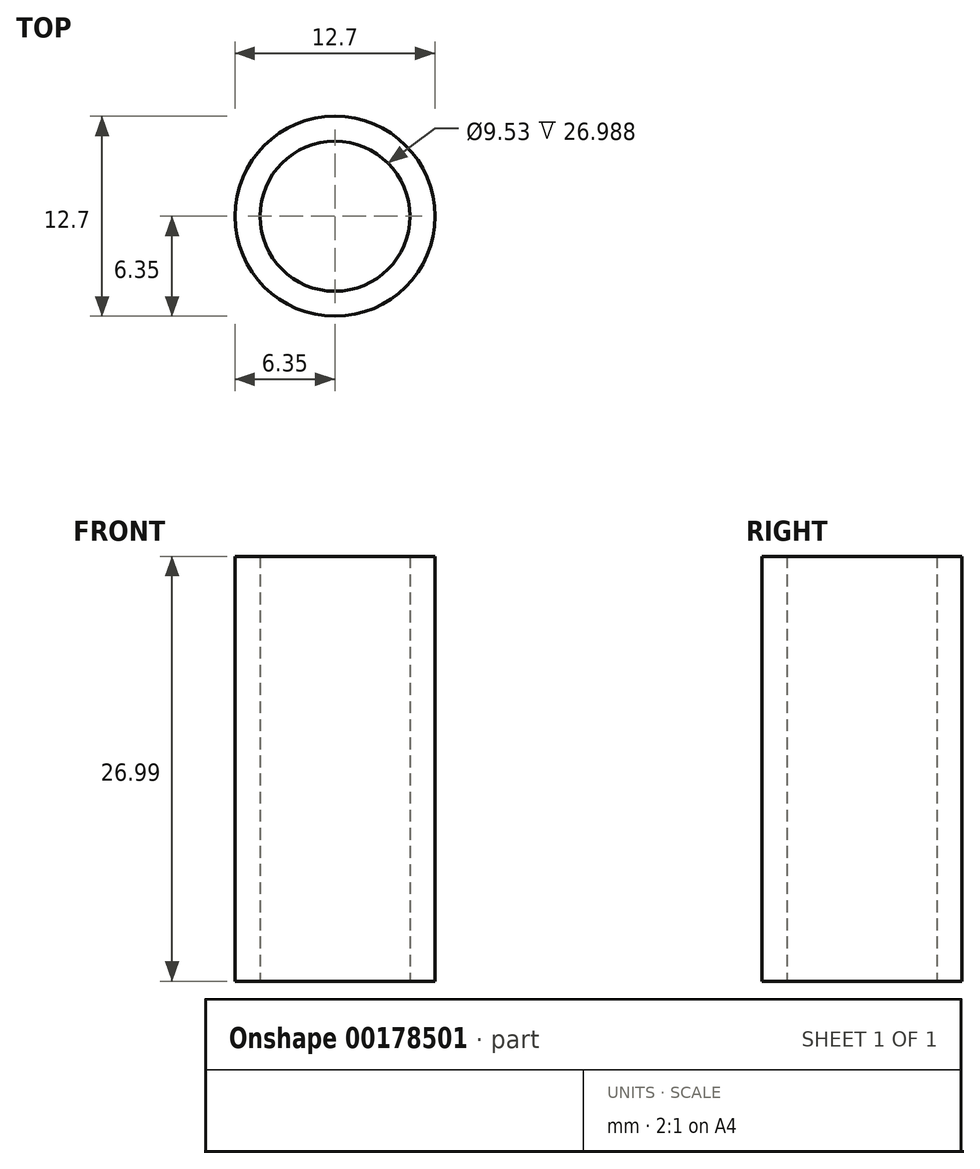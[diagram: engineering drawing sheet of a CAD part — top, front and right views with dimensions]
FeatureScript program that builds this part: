
annotation { "Feature Type Name" : "Feature", "Feature Type Description" : "" }
export const myFeature = defineFeature(function(context is Context, id is Id, definition is map)
    precondition{}
    {
        {
            var Q0;
            Q0=qCreatedBy(makeId("Top.planeOp"),FACE);
            var sketch = newSketch(context, id + "F0", { "sketchPlane" : qUnion([Q0])});
            skCircle(sketch, "E0", {"center": v(0, 0) * mm, "radius": 6.35 * mm});
            skCircle(sketch, "E1", {"center": v(0, 0) * mm, "radius": 4.76 * mm});
            skSolve(sketch);
        }
        {
            var Q0;
            Q0=makeQuery(id+"F0.imprint","IMPRINT",FACE,{"disambiguationData":[TD([[makeQuery(id+"F0.imprint","IMPRINT",EDGE,{"derivedFrom":sQuery(id+"F0.wireOp",EDGE,"E0")}),1.0]])]});
            extrude(context, id + "F1", {"entities" : qUnion([Q0]), "depth" : 26.99 * mm});
        }
    });
